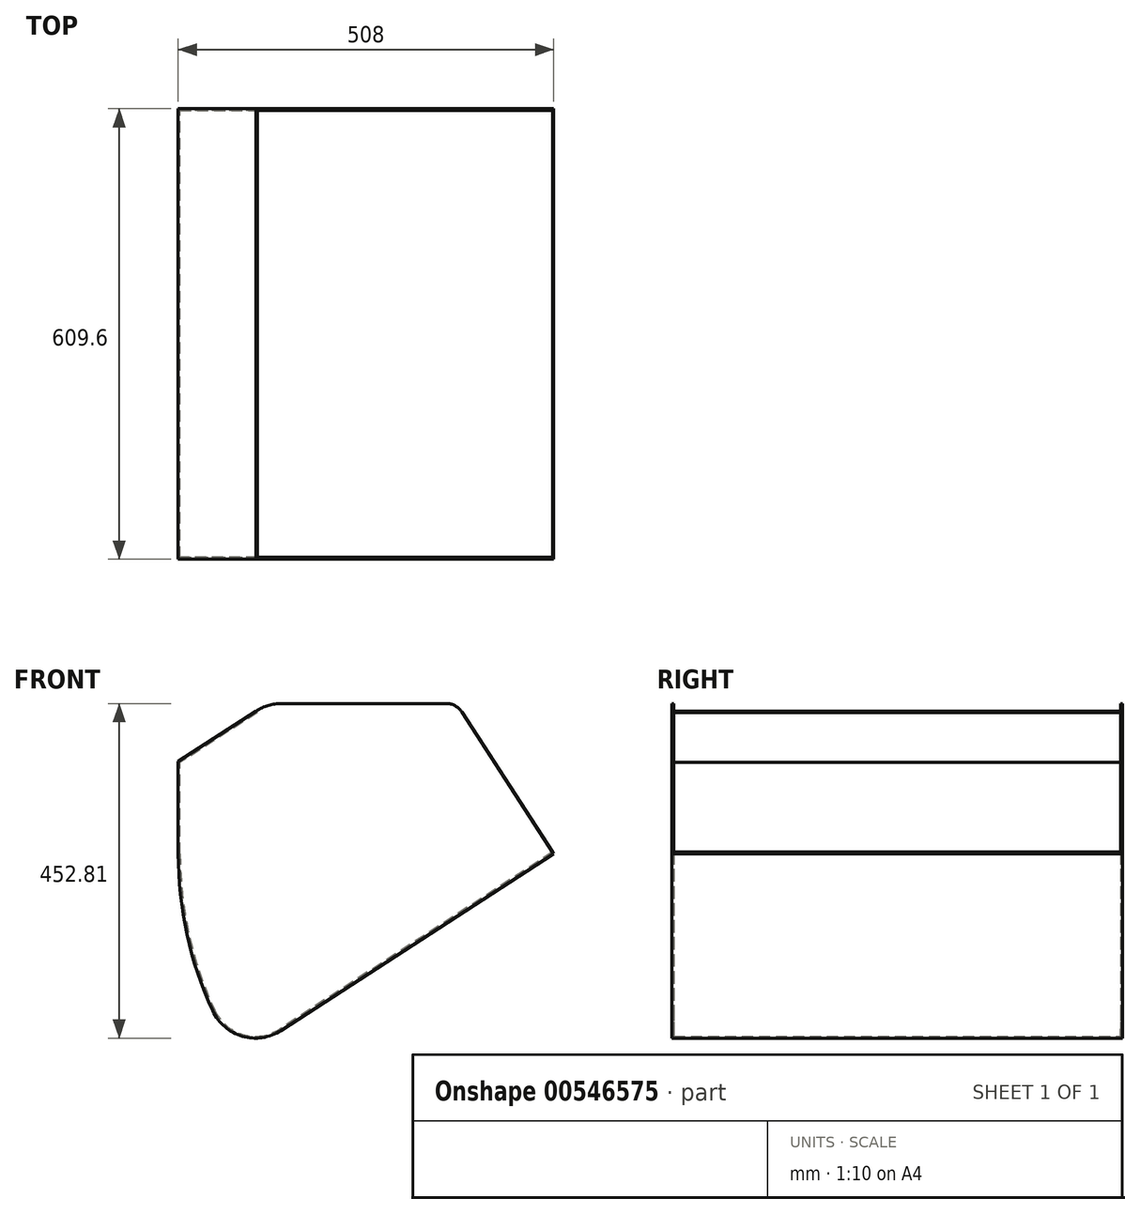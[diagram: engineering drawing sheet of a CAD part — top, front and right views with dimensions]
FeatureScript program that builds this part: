
annotation { "Feature Type Name" : "Feature", "Feature Type Description" : "" }
export const myFeature = defineFeature(function(context is Context, id is Id, definition is map)
    precondition{}
    {
        {
            var Q0;
            Q0=qCreatedBy(makeId("Front.planeOp"),FACE);
            var sketch = newSketch(context, id + "F0", { "sketchPlane" : qUnion([Q0])});
            skLineSegment(sketch, "E0.bottom", {"start": v(0, 0) * mm, "end": v(508, 0) * mm});
            skLineSegment(sketch, "E0.top", {"start": v(139.9, 457.2) * mm, "end": v(362.41, 457.2) * mm});
            skLineSegment(sketch, "E0.left", {"start": v(0, 10.27) * mm, "end": v(0, 457.2) * mm});
            skLineSegment(sketch, "E0.right", {"start": v(508, 0) * mm, "end": v(508, 254) * mm});
            skArc(sketch, "E1", {"start": v(342.53, 457.2) * mm, "mid": v(-151.84, 297.1) * mm, "end": v(318.32, 75.78) * mm});
            skPoint(sketch, "E2", {"position": v(508, 254) * mm});
            skLineSegment(sketch, "E3", {"start": v(540.45, 284.5) * mm, "end": v(318.32, 75.78) * mm});
            skLineSegment(sketch, "E4", {"start": v(540.45, 284.5) * mm, "end": v(540.45, 523.18) * mm});
            skLineSegment(sketch, "E5", {"start": v(508, 457.2) * mm, "end": v(617.65, 457.2) * mm});
            skLineSegment(sketch, "E6", {"start": v(515.21, 457.07) * mm, "end": v(508, 254) * mm});
            skLineSegment(sketch, "E7", {"start": v(0, 457.2) * mm, "end": v(72.96, 781.39) * mm});
            skPoint(sketch, "E8.visualSharp", {"position": v(0, 0) * mm});
            skArc(sketch, "E8.filletArc", {"start": v(0, 10.27) * mm, "mid": v(3.01, 4.87) * mm, "end": v(9.19, 4.6) * mm});
            skArc(sketch, "E9", {"start": v(25.84, 94.06) * mm, "mid": v(35.52, 67.39) * mm, "end": v(46.67, 41.3) * mm});
            skLineSegment(sketch, "E10", {"start": v(0, 30.53) * mm, "end": v(0, 381) * mm});
            skLineSegment(sketch, "E11", {"start": v(0, 381) * mm, "end": v(-68.97, 381) * mm});
            skLineSegment(sketch, "E12", {"start": v(508, 254) * mm, "end": v(383.72, 445.62) * mm});
            skArc(sketch, "E13.filletArc", {"start": v(383.72, 445.62) * mm, "mid": v(374.54, 454.12) * mm, "end": v(362.41, 457.2) * mm});
            skPoint(sketch, "E14.newPointB", {"position": v(127, 457.2) * mm});
            skArc(sketch, "E15.trimOffspring", {"start": v(0, 254) * mm, "mid": v(6.5, 173) * mm, "end": v(25.84, 94.06) * mm});
            skPoint(sketch, "E16.end.orphan", {"position": v(0, 330.2) * mm});
            skLineSegment(sketch, "E17", {"start": v(508, 254) * mm, "end": v(138.9, 14.61) * mm});
            skArc(sketch, "E18.trimOffspring", {"start": v(100.67, 557.56) * mm, "mid": v(52.43, 478.77) * mm, "end": v(19.26, 392.56) * mm});
            skPoint(sketch, "E19.visualSharp", {"position": v(81.79, -22.42) * mm});
            skArc(sketch, "E19.filletArc", {"start": v(46.67, 41.3) * mm, "mid": v(86.69, 6.9) * mm, "end": v(138.9, 14.61) * mm});
            skLineSegment(sketch, "E20.0", {"start": v(300.68, 573.66) * mm, "end": v(240.58, 534.67) * mm});
            skLineSegment(sketch, "E21.trimOffspring", {"start": v(105.36, 446.98) * mm, "end": v(0, 378.65) * mm});
            skPoint(sketch, "E22.visualSharp", {"position": v(121.12, 457.2) * mm});
            skArc(sketch, "E22.filletArc", {"start": v(139.9, 457.2) * mm, "mid": v(121.9, 454.6) * mm, "end": v(105.36, 446.98) * mm});
            skSolve(sketch);
        }
        {
            var Q0;
            {var subQ0=sQuery(id+"F0.wireOp",EDGE,"E0.left");var subQ1=sQuery(id+"F0.wireOp",EDGE,"E0.top");var subQ2=makeQuery(id+"F0.imprint","INTERSECT",VERTEX,{"derivedFrom":[subQ1,subQ0]});Q0=makeQuery(id+"F0.imprint","IMPRINT",FACE,{"disambiguationData":[TD([[makeQuery(id+"F0.imprint","IMPRINT",EDGE,{"disambiguationData":[TD([[subQ2,-1.0]])],"derivedFrom":subQ1}),-1.0]])]});}
            extrude(context, id + "F1", {"entities" : qUnion([Q0]), "depth" : 609.6 * mm, "offsetDistance" : 25.4 * mm});
        }
        {
            var Q0;
            Q0=makeQuery(id+"F1.opExtrude","SWEPT_FACE",FACE,{"disambiguationData":[OSD([sQuery(id+"F0.wireOp",EDGE,"E0.top")])]});
            var Q1;
            Q1=makeQuery(id+"F1.opExtrude","SWEPT_FACE",FACE,{"disambiguationData":[OSD([sQuery(id+"F0.wireOp",EDGE,"E13.filletArc")])]});
            var Q2;
            Q2=makeQuery(id+"F1.opExtrude","SWEPT_FACE",FACE,{"disambiguationData":[OSD([sQuery(id+"F0.wireOp",EDGE,"E12")])]});
            var Q3;
            Q3=makeQuery(id+"F1.opExtrude","SWEPT_FACE",FACE,{"disambiguationData":[OSD([sQuery(id+"F0.wireOp",EDGE,"E22.filletArc")])]});
            shell(context, id + "F2", {"entities" : qUnion([Q0, Q1, Q2, Q3]), "thickness" : 2.54 * mm});
        }
    });
